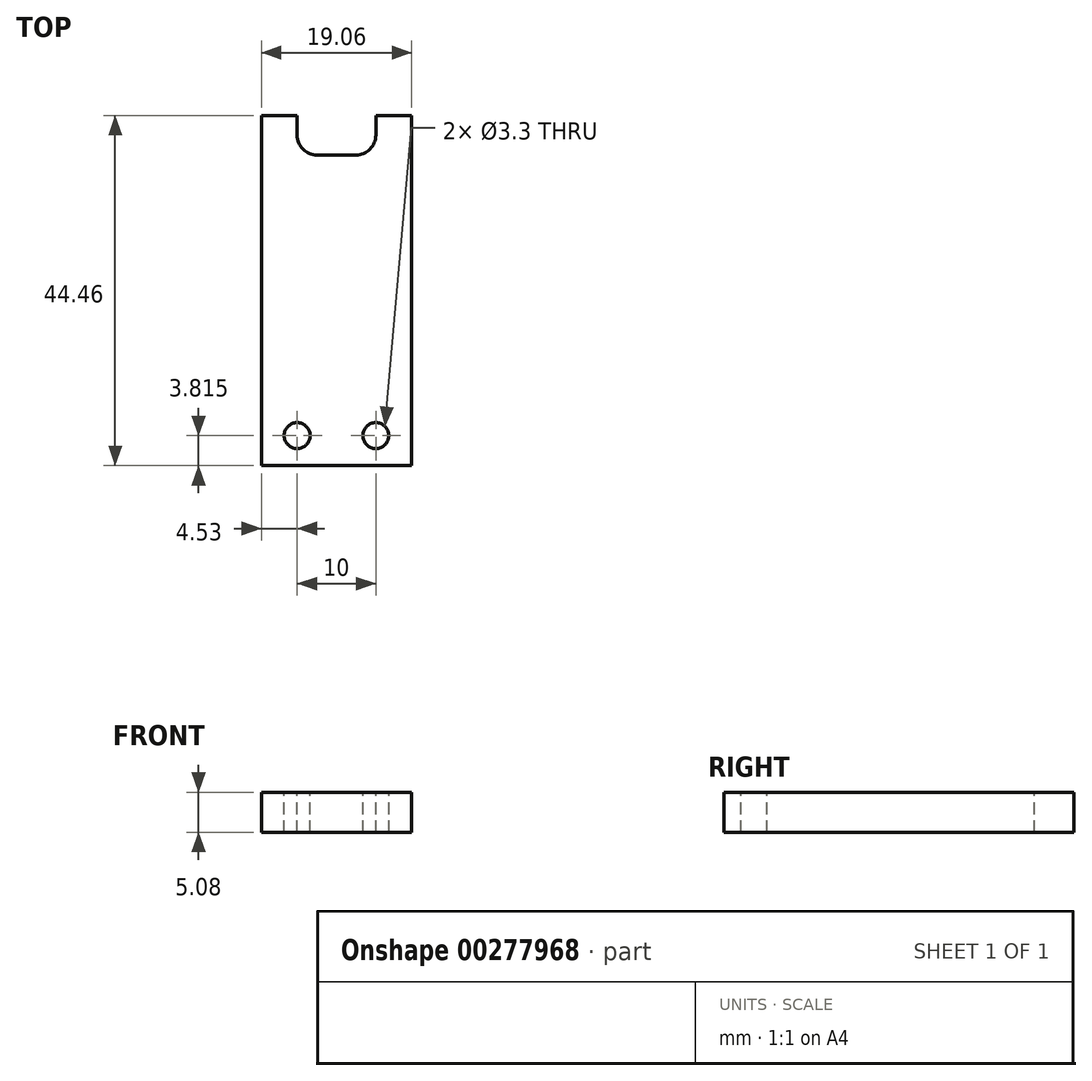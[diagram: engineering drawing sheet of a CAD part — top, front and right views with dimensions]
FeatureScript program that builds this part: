
annotation { "Feature Type Name" : "Feature", "Feature Type Description" : "" }
export const myFeature = defineFeature(function(context is Context, id is Id, definition is map)
    precondition{}
    {
        {
            var Q0;
            Q0=qCreatedBy(makeId("Top.planeOp"),FACE);
            var sketch = newSketch(context, id + "F0", { "sketchPlane" : qUnion([Q0])});
            skLineSegment(sketch, "E0.bottom", {"start": v(9.52, -22.23) * mm, "end": v(-9.53, -22.23) * mm});
            skLineSegment(sketch, "E0.top", {"start": v(9.53, 22.23) * mm, "end": v(-9.53, 22.23) * mm});
            skLineSegment(sketch, "E0.left", {"start": v(9.52, -22.23) * mm, "end": v(9.53, 22.23) * mm});
            skLineSegment(sketch, "E0.right", {"start": v(-9.53, -22.23) * mm, "end": v(-9.53, 22.23) * mm});
            skPoint(sketch, "E0.middle", {"position": v(0, 0) * mm});
            skSolve(sketch);
        }
        {
            var Q0;
            Q0=makeQuery(id+"F0.imprint","IMPRINT",FACE,{"disambiguationData":[TD([[makeQuery(id+"F0.imprint","IMPRINT",EDGE,{"derivedFrom":sQuery(id+"F0.wireOp",EDGE,"E0.bottom")}),-1.0]])]});
            extrude(context, id + "F1", {"entities" : qUnion([Q0]), "depth" : 5.08 * mm});
        }
        {
            var Q0;
            Q0=makeQuery(id+"F1.opExtrude","CAP_FACE",FACE,{"disambiguationData":[OSD([sQuery(id+"F0.wireOp",EDGE,"E0.bottom"),sQuery(id+"F0.wireOp",EDGE,"E0.top"),sQuery(id+"F0.wireOp",EDGE,"E0.left"),sQuery(id+"F0.wireOp",EDGE,"E0.right")])],"isStart":false});
            var sketch = newSketch(context, id + "F2", { "sketchPlane" : qUnion([Q0])});
            skLineSegment(sketch, "E1.bottom", {"start": v(5, 17.23) * mm, "end": v(-5, 17.23) * mm});
            skLineSegment(sketch, "E1.top", {"start": v(5, 27.22) * mm, "end": v(-5, 27.22) * mm});
            skLineSegment(sketch, "E1.left", {"start": v(5, 17.23) * mm, "end": v(5, 27.22) * mm});
            skLineSegment(sketch, "E1.right", {"start": v(-5, 17.23) * mm, "end": v(-5, 27.23) * mm});
            skPoint(sketch, "E1.middle", {"position": v(0, 22.23) * mm});
            skSolve(sketch);
        }
        {
            var Q0;
            {var subQ0=sQuery(id+"F2.wireOp",EDGE,"E1.top");Q0=makeQuery(id+"F2.imprint","IMPRINT",FACE,{"disambiguationData":[TD([[makeQuery(id+"F2.imprint","IMPRINT",EDGE,{"derivedFrom":subQ0}),1.0]])]});}
            var Q1;
            {var subQ0=sQuery(id+"F2.wireOp",EDGE,"E1.bottom");Q1=makeQuery(id+"F2.imprint","IMPRINT",FACE,{"disambiguationData":[TD([[makeQuery(id+"F2.imprint","IMPRINT",EDGE,{"derivedFrom":subQ0}),-1.0]])]});}
            extrude(context, id + "F3", {"entities" : qUnion([Q0, Q1]), "operationType" : NewBodyOperationType.REMOVE, "oppositeDirection" : true, "depth" : 25.4 * mm});
        }
        {
            var Q0;
            Q0=makeQuery(id+"F3.boolean.opBoolean","COPY",EDGE,{"derivedFrom":makeQuery(id+"F3.opExtrude","SWEPT_EDGE",EDGE,{"disambiguationData":[OSD([sQuery(id+"F2.wireOp",EDGE,"E1.bottom"),sQuery(id+"F2.wireOp",EDGE,"E1.right")])]})});
            var Q1;
            Q1=makeQuery(id+"F3.boolean.opBoolean","COPY",EDGE,{"derivedFrom":makeQuery(id+"F3.opExtrude","SWEPT_EDGE",EDGE,{"disambiguationData":[OSD([sQuery(id+"F2.wireOp",EDGE,"E1.bottom"),sQuery(id+"F2.wireOp",EDGE,"E1.left")])]})});
            fillet(context, id + "F4", {"entities" : qUnion([Q0, Q1]), "radius" : 2.54 * mm, "tangentPropagation" : true, "allowEdgeOverflow" : false});
        }
        {
            var Q0;
            Q0=makeQuery(id+"F1.opExtrude","CAP_FACE",FACE,{"disambiguationData":[OSD([sQuery(id+"F0.wireOp",EDGE,"E0.bottom"),sQuery(id+"F0.wireOp",EDGE,"E0.top"),sQuery(id+"F0.wireOp",EDGE,"E0.left"),sQuery(id+"F0.wireOp",EDGE,"E0.right")])],"isStart":false});
            var sketch = newSketch(context, id + "F5", { "sketchPlane" : qUnion([Q0])});
            skPoint(sketch, "E2", {"position": v(-5, -18.41) * mm});
            skPoint(sketch, "E3", {"position": v(5, -18.41) * mm});
            skSolve(sketch);
        }
        {
            var Q0;
            Q0=sQuery(id+"F5.wireOp",VERTEX,"E2");
            var Q1;
            Q1=sQuery(id+"F5.wireOp",VERTEX,"E3");
            var Q2;
            Q2=makeQuery(id+"F1.opExtrude","SWEPT_BODY",BODY,{"disambiguationData":[OSD([sQuery(id+"F0.wireOp",EDGE,"E0.bottom"),sQuery(id+"F0.wireOp",EDGE,"E0.top"),sQuery(id+"F0.wireOp",EDGE,"E0.left"),sQuery(id+"F0.wireOp",EDGE,"E0.right")])]});
            hole(context, id + "F6", {"style" : HoleStyle.SIMPLE, "endStyle" : HoleEndStyle.BLIND, "standardTappedOrClearance" : lookupTablePath({ "standard" : "ISO", "fit" : "Normal", "size" : "M3", "type" : "Clearance" }), "standardBlindInLast" : lookupTablePath({ "fit" : "Standard", "standard" : "ISO", "size" : "M3", "type" : "Clearance" }), "holeDiameter" : 3.3 * mm, "holeDepth" : 12.7 * mm, "tappedDepth" : 12.7 * mm, "tapClearance" : 3, "startFromSketch" : true, "locations" : qUnion([Q0, Q1]), "scope" : qUnion([Q2])});
        }
    });
